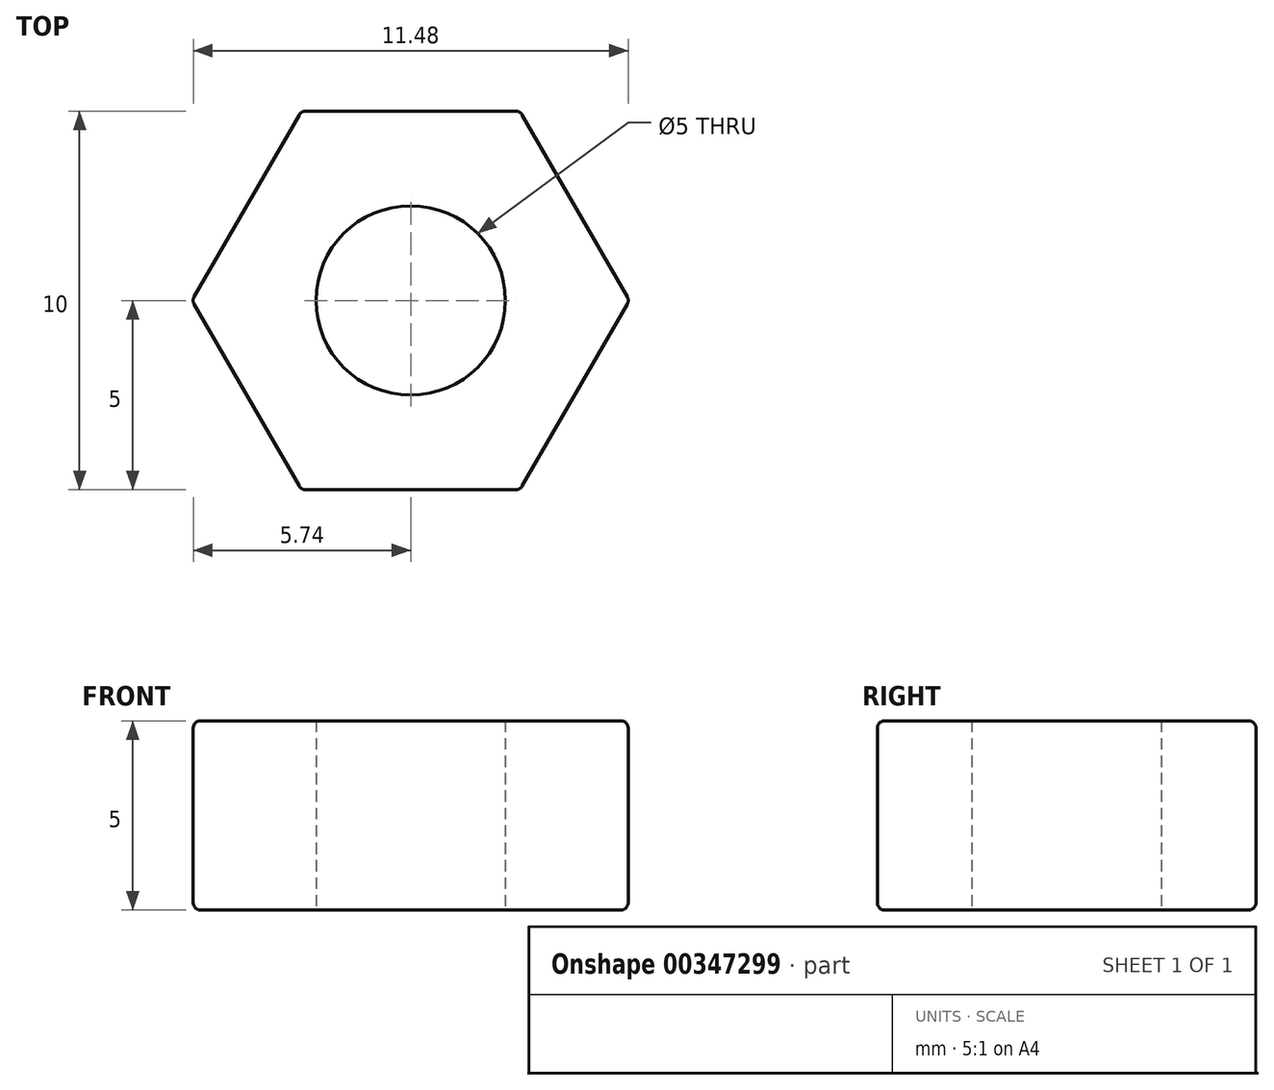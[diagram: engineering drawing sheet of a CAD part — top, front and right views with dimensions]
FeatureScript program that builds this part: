
annotation { "Feature Type Name" : "Feature", "Feature Type Description" : "" }
export const myFeature = defineFeature(function(context is Context, id is Id, definition is map)
    precondition{}
    {
        {
            var Q0;
            Q0=qCreatedBy(makeId("Top.planeOp"),FACE);
            var sketch = newSketch(context, id + "F0", { "sketchPlane" : qUnion([Q0])});
            skCircle(sketch, "E0.cCircle", {"center": v(0, 0) * mm, "radius": 5 * mm, "construction": true});
            skLineSegment(sketch, "E0.0", {"start": v(2.89, 5) * mm, "end": v(5.77, 0) * mm});
            skLineSegment(sketch, "E0.1", {"start": v(5.77, 0) * mm, "end": v(2.89, -5) * mm});
            skLineSegment(sketch, "E0.2", {"start": v(2.89, -5) * mm, "end": v(-2.89, -5) * mm});
            skLineSegment(sketch, "E0.3", {"start": v(-2.89, -5) * mm, "end": v(-5.77, 0) * mm});
            skLineSegment(sketch, "E0.4", {"start": v(-5.77, 0) * mm, "end": v(-2.89, 5) * mm});
            skLineSegment(sketch, "E0.5", {"start": v(-2.89, 5) * mm, "end": v(2.89, 5) * mm});
            skPoint(sketch, "E0.0.midPoint", {"position": v(4.33, 2.5) * mm});
            skCircle(sketch, "E1", {"center": v(0, 0) * mm, "radius": 2.5 * mm});
            skSolve(sketch);
        }
        {
            var Q0;
            Q0 = qSketchRegion(id + "F0", true);
            extrude(context, id + "F1", {"entities" : qUnion([Q0]), "depth" : 5 * mm});
        }
        {
            var Q0;
            Q0=makeQuery(id+"F1.opExtrude","SWEPT_FACE",FACE,{"disambiguationData":[OSD([sQuery(id+"F0.wireOp",EDGE,"E0.4")])]});
            var Q1;
            Q1=makeQuery(id+"F1.opExtrude","SWEPT_FACE",FACE,{"disambiguationData":[OSD([sQuery(id+"F0.wireOp",EDGE,"E0.3")])]});
            var Q2;
            Q2=makeQuery(id+"F1.opExtrude","SWEPT_FACE",FACE,{"disambiguationData":[OSD([sQuery(id+"F0.wireOp",EDGE,"E0.2")])]});
            var Q3;
            Q3=makeQuery(id+"F1.opExtrude","SWEPT_FACE",FACE,{"disambiguationData":[OSD([sQuery(id+"F0.wireOp",EDGE,"E0.1")])]});
            var Q4;
            Q4=makeQuery(id+"F1.opExtrude","SWEPT_FACE",FACE,{"disambiguationData":[OSD([sQuery(id+"F0.wireOp",EDGE,"E0.0")])]});
            var Q5;
            Q5=makeQuery(id+"F1.opExtrude","SWEPT_FACE",FACE,{"disambiguationData":[OSD([sQuery(id+"F0.wireOp",EDGE,"E0.5")])]});
            fillet(context, id + "F2", {"entities" : qUnion([Q0, Q1, Q2, Q3, Q4, Q5]), "radius" : 0.2 * mm, "tangentPropagation" : true, "allowEdgeOverflow" : false});
        }
    });
